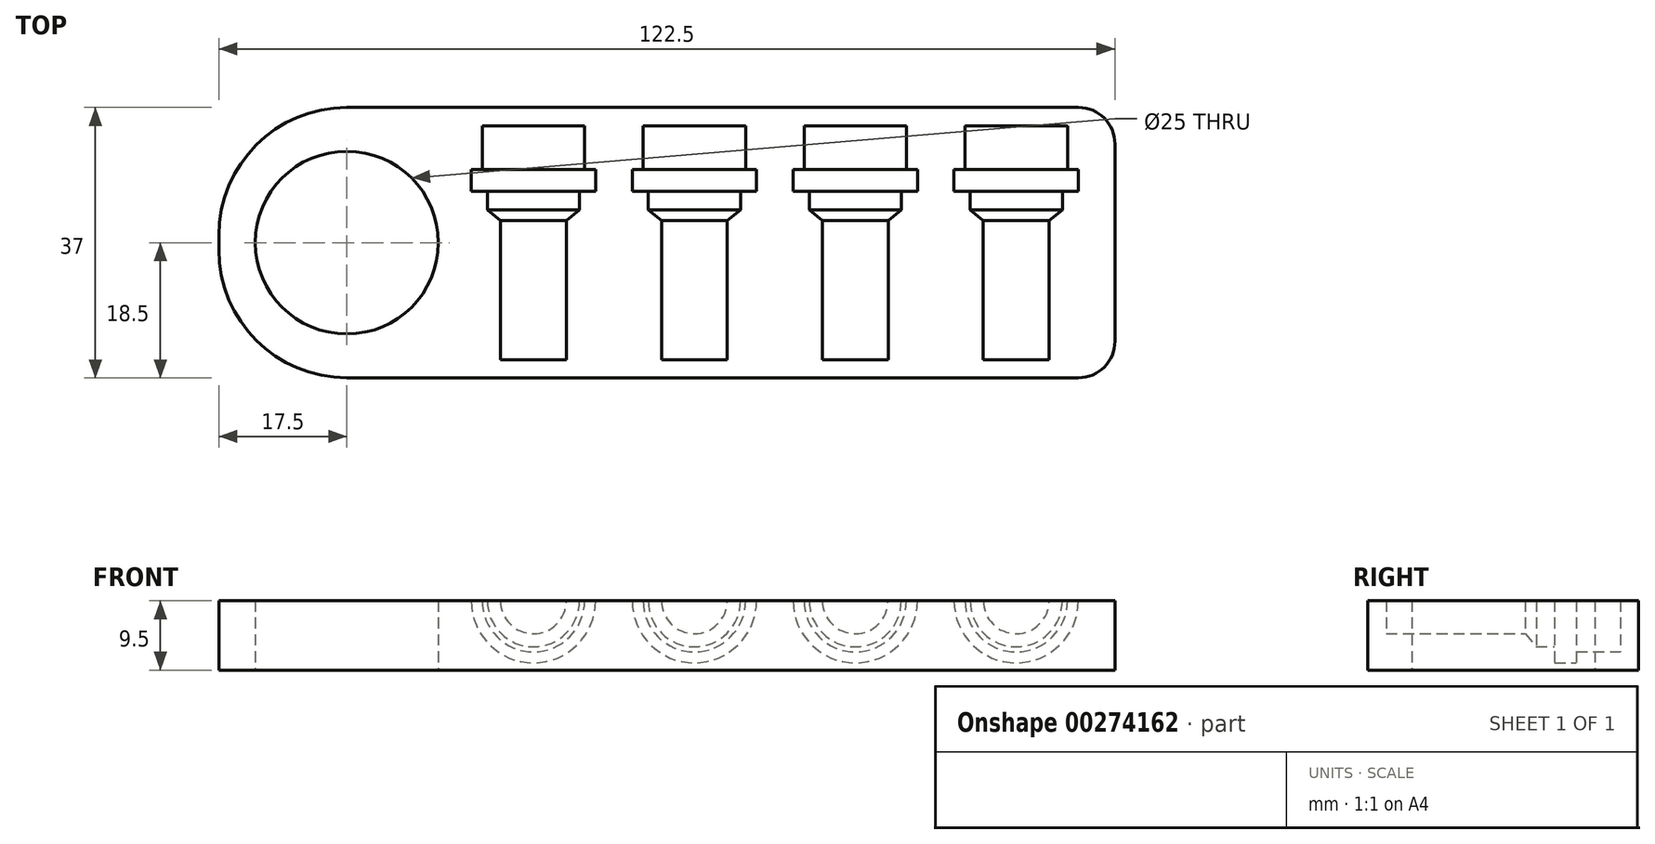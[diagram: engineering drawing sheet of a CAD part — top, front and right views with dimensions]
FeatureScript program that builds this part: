
annotation { "Feature Type Name" : "Feature", "Feature Type Description" : "" }
export const myFeature = defineFeature(function(context is Context, id is Id, definition is map)
    precondition{}
    {
        {
            var Q0;
            Q0=qCreatedBy(makeId("Top.planeOp"),FACE);
            var sketch = newSketch(context, id + "F0", { "sketchPlane" : qUnion([Q0])});
            skLineSegment(sketch, "E0.bottom", {"start": v(17.5, 0) * mm, "end": v(117.5, 0) * mm});
            skLineSegment(sketch, "E0.top", {"start": v(17.5, 37) * mm, "end": v(117.5, 37) * mm});
            skLineSegment(sketch, "E0.left", {"start": v(0, 17.5) * mm, "end": v(0, 19.5) * mm});
            skLineSegment(sketch, "E0.right", {"start": v(122.5, 5) * mm, "end": v(122.5, 32) * mm});
            skLineSegment(sketch, "E1.bottom", {"start": v(0, 0) * mm, "end": v(17.5, 0) * mm, "construction": true});
            skLineSegment(sketch, "E1.top", {"start": v(0, 18.5) * mm, "end": v(17.5, 18.5) * mm, "construction": true});
            skLineSegment(sketch, "E1.left", {"start": v(0, 0) * mm, "end": v(0, 18.5) * mm, "construction": true});
            skLineSegment(sketch, "E1.right", {"start": v(17.5, 0) * mm, "end": v(17.5, 18.5) * mm, "construction": true});
            skCircle(sketch, "E2", {"center": v(17.5, 18.5) * mm, "radius": 12.5 * mm});
            skPoint(sketch, "E3.visualSharp", {"position": v(0, 0) * mm});
            skArc(sketch, "E3.filletArc", {"start": v(0, 17.5) * mm, "mid": v(5.13, 5.13) * mm, "end": v(17.5, 0) * mm});
            skPoint(sketch, "E4.visualSharp", {"position": v(0, 37) * mm});
            skArc(sketch, "E4.filletArc", {"start": v(17.5, 37) * mm, "mid": v(5.13, 31.87) * mm, "end": v(0, 19.5) * mm});
            skPoint(sketch, "E5.visualSharp", {"position": v(122.5, 37) * mm});
            skArc(sketch, "E5.filletArc", {"start": v(122.5, 32) * mm, "mid": v(121.04, 35.54) * mm, "end": v(117.5, 37) * mm});
            skPoint(sketch, "E6.visualSharp", {"position": v(122.5, 0) * mm});
            skArc(sketch, "E6.filletArc", {"start": v(117.5, 0) * mm, "mid": v(121.04, 1.46) * mm, "end": v(122.5, 5) * mm});
            skSolve(sketch);
        }
        {
            var Q0;
            Q0=makeQuery(id+"F0.imprint","IMPRINT",FACE,{"disambiguationData":[TD([[makeQuery(id+"F0.imprint","IMPRINT",EDGE,{"derivedFrom":sQuery(id+"F0.wireOp",EDGE,"E0.bottom")}),1.0]])]});
            extrude(context, id + "F1", {"entities" : qUnion([Q0]), "depth" : 9.5 * mm});
        }
        {
            var Q0;
            Q0=makeQuery(id+"F1.opExtrude","CAP_FACE",FACE,{"disambiguationData":[OSD([sQuery(id+"F0.wireOp",EDGE,"E0.bottom"),sQuery(id+"F0.wireOp",EDGE,"E0.top"),sQuery(id+"F0.wireOp",EDGE,"E0.right"),sQuery(id+"F0.wireOp",EDGE,"E2"),sQuery(id+"F0.wireOp",EDGE,"E3.filletArc"),sQuery(id+"F0.wireOp",EDGE,"E4.filletArc"),sQuery(id+"F0.wireOp",EDGE,"E5.filletArc"),sQuery(id+"F0.wireOp",EDGE,"E6.filletArc")])],"isStart":false});
            var sketch = newSketch(context, id + "F2", { "sketchPlane" : qUnion([Q0])});
            skLineSegment(sketch, "E7.bottom", {"start": v(0, 0) * mm, "end": v(43, 0) * mm, "construction": true});
            skLineSegment(sketch, "E7.top", {"start": v(0, 2.5) * mm, "end": v(43, 2.5) * mm, "construction": true});
            skLineSegment(sketch, "E7.left", {"start": v(0, 0) * mm, "end": v(0, 2.5) * mm, "construction": true});
            skLineSegment(sketch, "E7.right", {"start": v(43, 0) * mm, "end": v(43, 2.5) * mm, "construction": true});
            skLineSegment(sketch, "E8", {"start": v(43, 2.5) * mm, "end": v(65, 2.5) * mm, "construction": true});
            skLineSegment(sketch, "E9", {"start": v(65, 2.5) * mm, "end": v(87, 2.5) * mm, "construction": true});
            skLineSegment(sketch, "E10", {"start": v(87, 2.5) * mm, "end": v(109, 2.5) * mm, "construction": true});
            skLineSegment(sketch, "E11.bottom", {"start": v(43, 2.5) * mm, "end": v(47.5, 2.5) * mm});
            skLineSegment(sketch, "E11.left", {"start": v(43, 2.5) * mm, "end": v(43, 21.5) * mm});
            skLineSegment(sketch, "E11.right", {"start": v(47.5, 2.5) * mm, "end": v(47.5, 21.5) * mm});
            skLineSegment(sketch, "E12.bottom", {"start": v(65, 2.5) * mm, "end": v(69.5, 2.5) * mm});
            skLineSegment(sketch, "E12.left", {"start": v(65, 2.5) * mm, "end": v(65, 21.5) * mm});
            skLineSegment(sketch, "E12.right", {"start": v(69.5, 2.5) * mm, "end": v(69.5, 21.5) * mm});
            skLineSegment(sketch, "E13.bottom", {"start": v(87, 2.5) * mm, "end": v(91.5, 2.5) * mm});
            skLineSegment(sketch, "E13.left", {"start": v(87, 2.5) * mm, "end": v(87, 21.5) * mm});
            skLineSegment(sketch, "E13.right", {"start": v(91.5, 2.5) * mm, "end": v(91.5, 21.5) * mm});
            skLineSegment(sketch, "E14.bottom", {"start": v(109, 2.5) * mm, "end": v(113.5, 2.5) * mm});
            skLineSegment(sketch, "E14.left", {"start": v(109, 2.5) * mm, "end": v(109, 21.5) * mm});
            skLineSegment(sketch, "E14.right", {"start": v(113.5, 2.5) * mm, "end": v(113.5, 21.5) * mm});
            skLineSegment(sketch, "E15", {"start": v(43, 21.5) * mm, "end": v(43, 23) * mm});
            skLineSegment(sketch, "E16", {"start": v(65, 21.5) * mm, "end": v(65, 23) * mm});
            skLineSegment(sketch, "E17", {"start": v(87, 21.5) * mm, "end": v(87, 23) * mm});
            skLineSegment(sketch, "E18", {"start": v(109, 21.5) * mm, "end": v(109, 23) * mm});
            skLineSegment(sketch, "E19.left", {"start": v(43, 23) * mm, "end": v(43, 25.5) * mm});
            skLineSegment(sketch, "E19.right", {"start": v(49.3, 23) * mm, "end": v(49.3, 25.5) * mm});
            skLineSegment(sketch, "E20.left", {"start": v(65, 23) * mm, "end": v(65, 25.5) * mm});
            skLineSegment(sketch, "E20.right", {"start": v(71.3, 23) * mm, "end": v(71.3, 25.5) * mm});
            skLineSegment(sketch, "E21.left", {"start": v(87, 23) * mm, "end": v(87, 25.5) * mm});
            skLineSegment(sketch, "E21.right", {"start": v(93.3, 23) * mm, "end": v(93.3, 25.5) * mm});
            skLineSegment(sketch, "E22.left", {"start": v(109, 23) * mm, "end": v(109, 25.5) * mm});
            skLineSegment(sketch, "E22.right", {"start": v(115.3, 23) * mm, "end": v(115.3, 25.5) * mm});
            skLineSegment(sketch, "E23.bottom", {"start": v(49.3, 25.5) * mm, "end": v(51.5, 25.5) * mm});
            skLineSegment(sketch, "E23.top", {"start": v(50, 28.5) * mm, "end": v(51.5, 28.5) * mm});
            skLineSegment(sketch, "E23.left", {"start": v(43, 25.5) * mm, "end": v(43, 28.5) * mm});
            skLineSegment(sketch, "E23.right", {"start": v(51.5, 25.5) * mm, "end": v(51.5, 28.5) * mm});
            skLineSegment(sketch, "E24.bottom", {"start": v(71.3, 25.5) * mm, "end": v(73.5, 25.5) * mm});
            skLineSegment(sketch, "E24.top", {"start": v(72, 28.5) * mm, "end": v(73.5, 28.5) * mm});
            skLineSegment(sketch, "E24.left", {"start": v(65, 25.5) * mm, "end": v(65, 28.5) * mm});
            skLineSegment(sketch, "E24.right", {"start": v(73.5, 25.5) * mm, "end": v(73.5, 28.5) * mm});
            skLineSegment(sketch, "E25.bottom", {"start": v(93.3, 25.5) * mm, "end": v(95.5, 25.5) * mm});
            skLineSegment(sketch, "E25.top", {"start": v(94, 28.5) * mm, "end": v(95.5, 28.5) * mm});
            skLineSegment(sketch, "E25.left", {"start": v(87, 25.5) * mm, "end": v(87, 28.5) * mm});
            skLineSegment(sketch, "E25.right", {"start": v(95.5, 25.5) * mm, "end": v(95.5, 28.5) * mm});
            skLineSegment(sketch, "E26.bottom", {"start": v(115.3, 25.5) * mm, "end": v(117.5, 25.5) * mm});
            skLineSegment(sketch, "E26.top", {"start": v(116, 28.5) * mm, "end": v(117.5, 28.5) * mm});
            skLineSegment(sketch, "E26.left", {"start": v(109, 25.5) * mm, "end": v(109, 28.5) * mm});
            skLineSegment(sketch, "E26.right", {"start": v(117.5, 25.5) * mm, "end": v(117.5, 28.5) * mm});
            skLineSegment(sketch, "E27.top", {"start": v(109, 34.5) * mm, "end": v(116, 34.5) * mm});
            skLineSegment(sketch, "E27.left", {"start": v(109, 28.5) * mm, "end": v(109, 34.5) * mm});
            skLineSegment(sketch, "E27.right", {"start": v(116, 28.5) * mm, "end": v(116, 34.5) * mm});
            skLineSegment(sketch, "E28.top", {"start": v(87, 34.5) * mm, "end": v(94, 34.5) * mm});
            skLineSegment(sketch, "E28.left", {"start": v(87, 28.5) * mm, "end": v(87, 34.5) * mm});
            skLineSegment(sketch, "E28.right", {"start": v(94, 28.5) * mm, "end": v(94, 34.5) * mm});
            skLineSegment(sketch, "E29.top", {"start": v(65, 34.5) * mm, "end": v(72, 34.5) * mm});
            skLineSegment(sketch, "E29.left", {"start": v(65, 28.5) * mm, "end": v(65, 34.5) * mm});
            skLineSegment(sketch, "E29.right", {"start": v(72, 28.5) * mm, "end": v(72, 34.5) * mm});
            skLineSegment(sketch, "E30.top", {"start": v(43, 34.5) * mm, "end": v(50, 34.5) * mm});
            skLineSegment(sketch, "E30.left", {"start": v(43, 28.5) * mm, "end": v(43, 34.5) * mm});
            skLineSegment(sketch, "E30.right", {"start": v(50, 28.5) * mm, "end": v(50, 34.5) * mm});
            skLineSegment(sketch, "E31", {"start": v(47.5, 21.5) * mm, "end": v(49.3, 23) * mm});
            skLineSegment(sketch, "E32", {"start": v(69.5, 21.5) * mm, "end": v(71.3, 23) * mm});
            skLineSegment(sketch, "E33", {"start": v(91.5, 21.5) * mm, "end": v(93.3, 23) * mm});
            skLineSegment(sketch, "E34", {"start": v(113.5, 21.5) * mm, "end": v(115.3, 23) * mm});
            skSolve(sketch);
        }
        {
            var Q0;
            Q0=makeQuery(id+"F2.imprint","IMPRINT",FACE,{"disambiguationData":[TD([[makeQuery(id+"F2.imprint","IMPRINT",EDGE,{"derivedFrom":sQuery(id+"F2.wireOp",EDGE,"E14.bottom")}),1.0]])]});
            var Q1;
            Q1=sQuery(id+"F2.wireOp",EDGE,"E14.left");
            revolve(context, id + "F3", {"operationType" : NewBodyOperationType.REMOVE, "entities" : qUnion([Q0]), "axis" : qUnion([Q1]), "revolveType" : RevolveType.FULL, "oppositeDirection" : true});
        }
        {
            var Q0;
            Q0=makeQuery(id+"F2.imprint","IMPRINT",FACE,{"disambiguationData":[TD([[makeQuery(id+"F2.imprint","IMPRINT",EDGE,{"derivedFrom":sQuery(id+"F2.wireOp",EDGE,"E13.bottom")}),1.0]])]});
            var Q1;
            Q1=sQuery(id+"F2.wireOp",EDGE,"E13.left");
            revolve(context, id + "F4", {"operationType" : NewBodyOperationType.REMOVE, "entities" : qUnion([Q0]), "axis" : qUnion([Q1]), "revolveType" : RevolveType.FULL, "oppositeDirection" : true});
        }
        {
            var Q0;
            Q0=makeQuery(id+"F2.imprint","IMPRINT",FACE,{"disambiguationData":[TD([[makeQuery(id+"F2.imprint","IMPRINT",EDGE,{"derivedFrom":sQuery(id+"F2.wireOp",EDGE,"E12.bottom")}),1.0]])]});
            var Q1;
            Q1=sQuery(id+"F2.wireOp",EDGE,"E12.left");
            revolve(context, id + "F5", {"operationType" : NewBodyOperationType.REMOVE, "entities" : qUnion([Q0]), "axis" : qUnion([Q1]), "revolveType" : RevolveType.FULL, "oppositeDirection" : true});
        }
        {
            var Q0;
            Q0=makeQuery(id+"F2.imprint","IMPRINT",FACE,{"disambiguationData":[TD([[makeQuery(id+"F2.imprint","IMPRINT",EDGE,{"derivedFrom":sQuery(id+"F2.wireOp",EDGE,"E11.bottom")}),1.0]])]});
            var Q1;
            Q1=sQuery(id+"F2.wireOp",EDGE,"E11.left");
            revolve(context, id + "F6", {"operationType" : NewBodyOperationType.REMOVE, "entities" : qUnion([Q0]), "axis" : qUnion([Q1]), "revolveType" : RevolveType.FULL, "oppositeDirection" : true});
        }
    });
